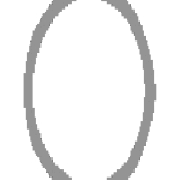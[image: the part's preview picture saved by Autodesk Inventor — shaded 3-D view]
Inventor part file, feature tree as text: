
AUTODESK INVENTOR PART (.ipt)
format: ipt  version: 2021 (Build 250183000, 183)  size: 114,688 bytes
history: native  units: in
note: dims shown in document units (in); Inventor stores cm internally (conversion verified against a paired STEP export)
features: other x4, sketch x3, plane x1
ambient origin geometry x8: Origin, YZ Plane, XZ Plane, XY Plane, X Axis, Y Axis, Z Axis, Center Point
bodies: Solid1 (feature_tree), Body (feature_tree)
feature tree (8):
  other  "Driven Length"
  other  "Frame Generator"
  other  "Start Plane"
  other  "End Plane"
  sketch  "Sketch"  dims[d2=4.559in d4=-0.0in d5=4.559in d6=0.12in d7=0.0in d8=90.0deg d9=4.559in]
  sketch  "Sketch2"  dims[d0=1.0in]
  plane  "Work Plane3"
  sketch  "Sketch3"  dims[d1=0.065in]
